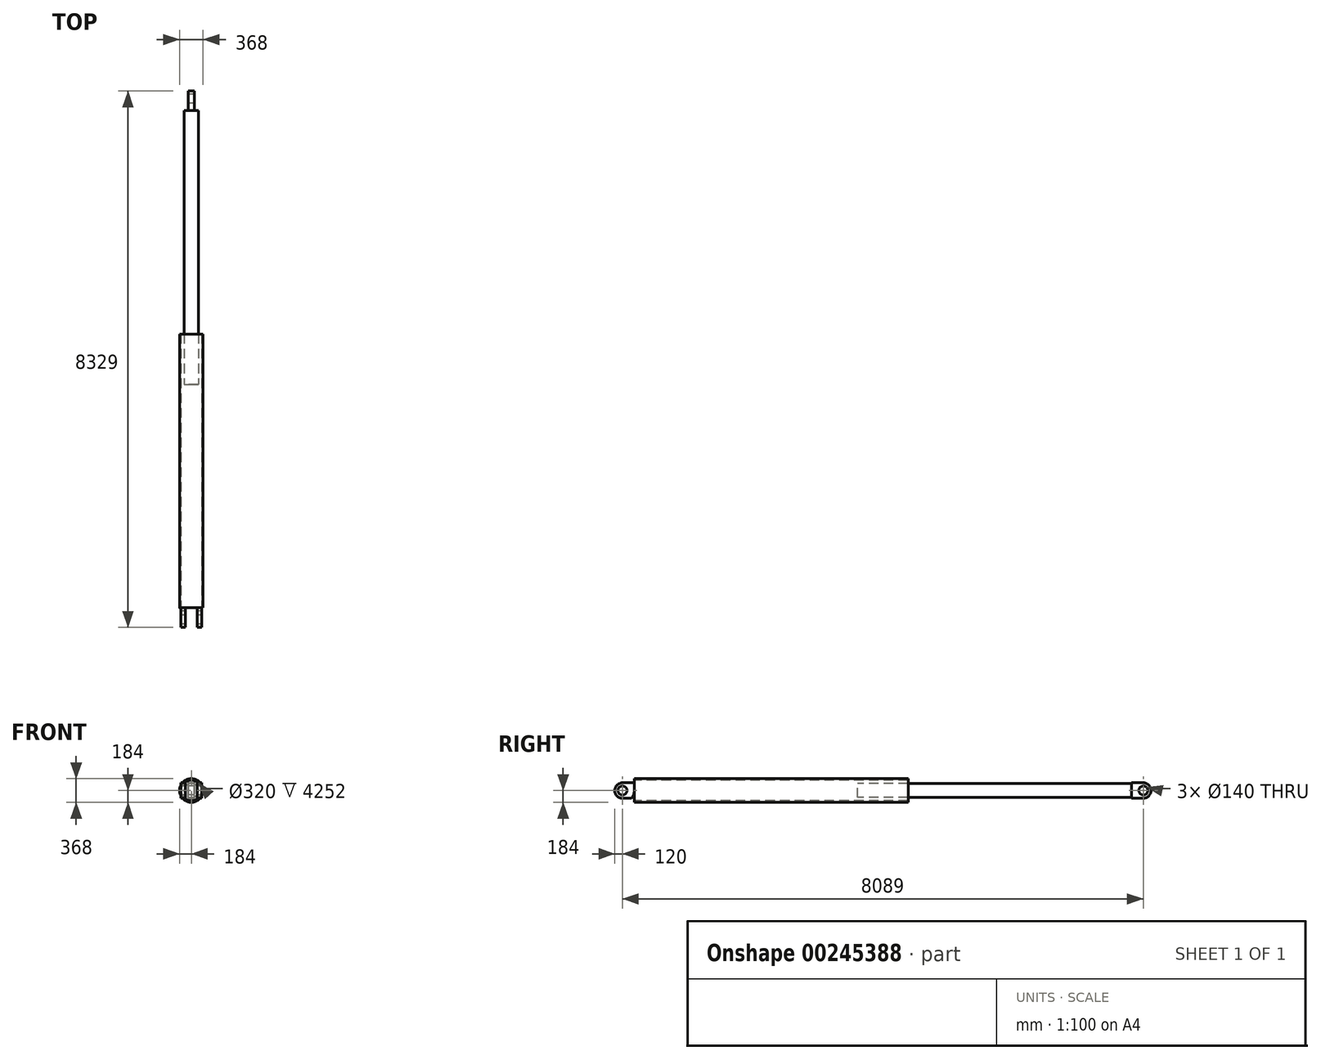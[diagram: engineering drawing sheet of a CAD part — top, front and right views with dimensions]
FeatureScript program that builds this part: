
annotation { "Feature Type Name" : "Feature", "Feature Type Description" : "" }
export const myFeature = defineFeature(function(context is Context, id is Id, definition is map)
    precondition{}
    {
        {
            var Q0;
            Q0=qCreatedBy(makeId("Right.planeOp"),FACE);
            var sketch = newSketch(context, id + "F0", { "sketchPlane" : qUnion([Q0])});
            skCircle(sketch, "E0", {"center": v(0, 0) * mm, "radius": 70 * mm});
            skCircle(sketch, "E1", {"center": v(0, 0) * mm, "radius": 184 * mm});
            skCircle(sketch, "E2", {"center": v(8089, 0) * mm, "radius": 70 * mm});
            skCircle(sketch, "E3", {"center": v(8089, 0) * mm, "radius": 184 * mm});
            skLineSegment(sketch, "E4", {"start": v(0, 0) * mm, "end": v(0, 70) * mm, "construction": true});
            skLineSegment(sketch, "E5", {"start": v(0, 70) * mm, "end": v(0, 184) * mm, "construction": true});
            skLineSegment(sketch, "E6", {"start": v(0, 0) * mm, "end": v(8089, 0) * mm, "construction": true});
            skLineSegment(sketch, "E7", {"start": v(184, 184) * mm, "end": v(184, -184) * mm});
            skLineSegment(sketch, "E8", {"start": v(0, -184) * mm, "end": v(184, -184) * mm});
            skLineSegment(sketch, "E9", {"start": v(184, 184) * mm, "end": v(0, 184) * mm});
            skLineSegment(sketch, "E10", {"start": v(8089, 184) * mm, "end": v(7905, 184) * mm});
            skLineSegment(sketch, "E11", {"start": v(7905, 184) * mm, "end": v(7905, -184) * mm});
            skLineSegment(sketch, "E12", {"start": v(8089, -184) * mm, "end": v(7905, -184) * mm});
            skLineSegment(sketch, "E13", {"start": v(8089, 0) * mm, "end": v(8089, 70) * mm, "construction": true});
            skLineSegment(sketch, "E14.bottom", {"start": v(184, 0) * mm, "end": v(4436, 0) * mm});
            skLineSegment(sketch, "E14.top", {"start": v(184, 184) * mm, "end": v(4436, 184) * mm});
            skLineSegment(sketch, "E14.left", {"start": v(184, 0) * mm, "end": v(184, 184) * mm});
            skLineSegment(sketch, "E14.right", {"start": v(4436, 0) * mm, "end": v(4436, 184) * mm});
            skLineSegment(sketch, "E15.top", {"start": v(184, 160) * mm, "end": v(4436, 160) * mm});
            skLineSegment(sketch, "E15.left", {"start": v(184, 0) * mm, "end": v(184, 160) * mm});
            skLineSegment(sketch, "E16.top", {"start": v(4436, 0) * mm, "end": v(7905, 0) * mm});
            skLineSegment(sketch, "E17", {"start": v(4436, 184) * mm, "end": v(4620, 184) * mm, "construction": true});
            skLineSegment(sketch, "E18", {"start": v(7905, -110) * mm, "end": v(3653, -110) * mm});
            skLineSegment(sketch, "E19", {"start": v(3653, -110) * mm, "end": v(3469, -110) * mm, "construction": true});
            skLineSegment(sketch, "E20", {"start": v(3653, -110) * mm, "end": v(3653, 0) * mm});
            skLineSegment(sketch, "E21", {"start": v(0, -621.93) * mm, "end": v(4620, -621.93) * mm, "construction": true});
            skLineSegment(sketch, "E22", {"start": v(3469, -428.69) * mm, "end": v(8089, -428.69) * mm, "construction": true});
            skSolve(sketch);
        }
        {
            var Q0;
            Q0=makeQuery(id+"F0.imprint","IMPRINT",FACE,{"disambiguationData":[TD([[makeQuery(id+"F0.imprint","IMPRINT",EDGE,{"derivedFrom":sQuery(id+"F0.wireOp",EDGE,"E14.top")}),-1.0]])]});
            var Q1;
            Q1=sQuery(id+"F0.wireOp",EDGE,"E14.bottom");
            revolve(context, id + "F1", {"entities" : qUnion([Q0]), "axis" : qUnion([Q1]), "revolveType" : RevolveType.FULL});
        }
        {
            var Q0;
            {var subQ1=sQuery(id+"F0.wireOp",EDGE,"E16.top");Q0=makeQuery(id+"F0.imprint","IMPRINT",FACE,{"disambiguationData":[TD([[makeQuery(id+"F0.imprint","IMPRINT",EDGE,{"derivedFrom":subQ1}),-1.0]])]});}
            var Q1;
            Q1=sQuery(id+"F0.wireOp",EDGE,"E16.top");
            revolve(context, id + "F2", {"surfaceOperationType" : NewSurfaceOperationType.NEW, "entities" : qUnion([Q0]), "axis" : qUnion([Q1]), "revolveType" : RevolveType.FULL});
        }
        {
            var Q0;
            Q0=makeQuery(id+"F0.imprint","IMPRINT",FACE,{"disambiguationData":[TD([[makeQuery(id+"F0.imprint","IMPRINT",EDGE,{"derivedFrom":sQuery(id+"F0.wireOp",EDGE,"E0")}),-1.0]])]});
            var Q1;
            {var subQ2=sQuery(id+"F0.wireOp",EDGE,"E9");Q1=makeQuery(id+"F0.imprint","IMPRINT",FACE,{"disambiguationData":[TD([[makeQuery(id+"F0.imprint","IMPRINT",EDGE,{"derivedFrom":subQ2}),1.0]])]});}
            var Q2;
            {var subQ0=sQuery(id+"F0.wireOp",EDGE,"E7");Q2=makeQuery(id+"F0.imprint","IMPRINT",FACE,{"disambiguationData":[TD([[makeQuery(id+"F0.imprint","IMPRINT",EDGE,{"derivedFrom":subQ0}),-1.0]])]});}
            extrude(context, id + "F3", {"entities" : qUnion([Q0, Q1, Q2]), "operationType" : NewBodyOperationType.ADD, "endBound" : BoundingType.SYMMETRIC, "offsetDistance" : 25 * mm, "depth" : 330 * mm});
        }
        {
            var Q0;
            Q0=makeQuery(id+"F0.imprint","IMPRINT",FACE,{"disambiguationData":[TD([[makeQuery(id+"F0.imprint","IMPRINT",EDGE,{"derivedFrom":sQuery(id+"F0.wireOp",EDGE,"E2")}),-1.0]])]});
            var Q1;
            {var subQ0=sQuery(id+"F0.wireOp",EDGE,"E10");Q1=makeQuery(id+"F0.imprint","IMPRINT",FACE,{"disambiguationData":[TD([[makeQuery(id+"F0.imprint","IMPRINT",EDGE,{"derivedFrom":subQ0}),1.0]])]});}
            var Q2;
            {var subQ0=sQuery(id+"F0.wireOp",EDGE,"E12");Q2=makeQuery(id+"F0.imprint","IMPRINT",FACE,{"disambiguationData":[TD([[makeQuery(id+"F0.imprint","IMPRINT",EDGE,{"derivedFrom":subQ0}),-1.0]])]});}
            extrude(context, id + "F4", {"entities" : qUnion([Q0, Q1, Q2]), "operationType" : NewBodyOperationType.ADD, "endBound" : BoundingType.SYMMETRIC, "offsetDistance" : 25 * mm, "depth" : 100 * mm});
        }
        {
            var Q0;
            {var subQ0=sQuery(id+"F0.wireOp",EDGE,"E15.top");Q0=makeQuery(id+"F0.imprint","IMPRINT",FACE,{"disambiguationData":[TD([[makeQuery(id+"F0.imprint","IMPRINT",EDGE,{"derivedFrom":subQ0}),-1.0]])]});}
            var Q1;
            Q1=sQuery(id+"F0.wireOp",EDGE,"E14.bottom");
            revolve(context, id + "F5", {"surfaceOperationType" : NewSurfaceOperationType.NEW, "entities" : qUnion([Q0]), "axis" : qUnion([Q1]), "revolveType" : RevolveType.FULL});
        }
        {
            var Q0;
            Q0=makeQuery(id+"F0.imprint","IMPRINT",FACE,{"disambiguationData":[TD([[makeQuery(id+"F0.imprint","IMPRINT",EDGE,{"derivedFrom":sQuery(id+"F0.wireOp",EDGE,"E0")}),-1.0]])]});
            var Q1;
            {var subQ2=sQuery(id+"F0.wireOp",EDGE,"E9");Q1=makeQuery(id+"F0.imprint","IMPRINT",FACE,{"disambiguationData":[TD([[makeQuery(id+"F0.imprint","IMPRINT",EDGE,{"derivedFrom":subQ2}),1.0]])]});}
            var Q2;
            {var subQ0=sQuery(id+"F0.wireOp",EDGE,"E7");Q2=makeQuery(id+"F0.imprint","IMPRINT",FACE,{"disambiguationData":[TD([[makeQuery(id+"F0.imprint","IMPRINT",EDGE,{"derivedFrom":subQ0}),-1.0]])]});}
            extrude(context, id + "F6", {"entities" : qUnion([Q0, Q1, Q2]), "operationType" : NewBodyOperationType.REMOVE, "endBound" : BoundingType.SYMMETRIC, "oppositeDirection" : true, "depth" : 190 * mm, "offsetDistance" : 25 * mm});
        }
        {
            var Q0;
            Q0=makeQuery(id+"F3.opExtrude","CAP_FACE",FACE,{"disambiguationData":[OSD([sQuery(id+"F0.wireOp",EDGE,"E0"),sQuery(id+"F0.wireOp",EDGE,"E1"),sQuery(id+"F0.wireOp",EDGE,"E7"),sQuery(id+"F0.wireOp",EDGE,"E8"),sQuery(id+"F0.wireOp",EDGE,"E9"),sQuery(id+"F0.wireOp",EDGE,"E14.left"),sQuery(id+"F0.wireOp",EDGE,"E15.left")])],"isStart":false});
            var sketch = newSketch(context, id + "F7", { "sketchPlane" : qUnion([Q0])});
            skCircle(sketch, "E23", {"center": v(0, 0) * mm, "radius": 120 * mm});
            skLineSegment(sketch, "E24", {"start": v(0, 120) * mm, "end": v(184, 120) * mm});
            skLineSegment(sketch, "E25", {"start": v(0, -120) * mm, "end": v(184, -120) * mm});
            skLineSegment(sketch, "E26", {"start": v(184, -120) * mm, "end": v(184, 120) * mm});
            skSolve(sketch);
        }
        {
            var Q0;
            {var subQ2=sQuery(id+"F7.wireOp",EDGE,"E24");Q0=makeQuery(id+"F7.imprint","IMPRINT",FACE,{"disambiguationData":[TD([[makeQuery(id+"F7.imprint","IMPRINT",EDGE,{"derivedFrom":subQ2}),1.0]])]});}
            extrude(context, id + "F8", {"entities" : qUnion([Q0]), "operationType" : NewBodyOperationType.REMOVE, "endBound" : BoundingType.THROUGH_ALL, "oppositeDirection" : true, "depth" : 25 * mm, "offsetDistance" : 25 * mm});
        }
        {
            var Q0;
            Q0=makeQuery(id+"F4.opExtrude","CAP_FACE",FACE,{"disambiguationData":[OSD([sQuery(id+"F0.wireOp",EDGE,"E2"),sQuery(id+"F0.wireOp",EDGE,"E3"),sQuery(id+"F0.wireOp",EDGE,"E10"),sQuery(id+"F0.wireOp",EDGE,"E11"),sQuery(id+"F0.wireOp",EDGE,"E12")])],"isStart":false});
            var sketch = newSketch(context, id + "F9", { "sketchPlane" : qUnion([Q0])});
            skCircle(sketch, "E27", {"center": v(8089, 0) * mm, "radius": 120 * mm});
            skLineSegment(sketch, "E28", {"start": v(8089, 120) * mm, "end": v(7905, 120) * mm});
            skLineSegment(sketch, "E29", {"start": v(8089, -120) * mm, "end": v(7905, -120) * mm});
            skSolve(sketch);
        }
        {
            var Q0;
            {var subQ2=sQuery(id+"F9.wireOp",EDGE,"E28");Q0=makeQuery(id+"F9.imprint","IMPRINT",FACE,{"disambiguationData":[TD([[makeQuery(id+"F9.imprint","IMPRINT",EDGE,{"derivedFrom":subQ2}),-1.0]])]});}
            extrude(context, id + "F10", {"entities" : qUnion([Q0]), "operationType" : NewBodyOperationType.REMOVE, "endBound" : BoundingType.THROUGH_ALL, "oppositeDirection" : true, "depth" : 25 * mm, "offsetDistance" : 25 * mm});
        }
    });
